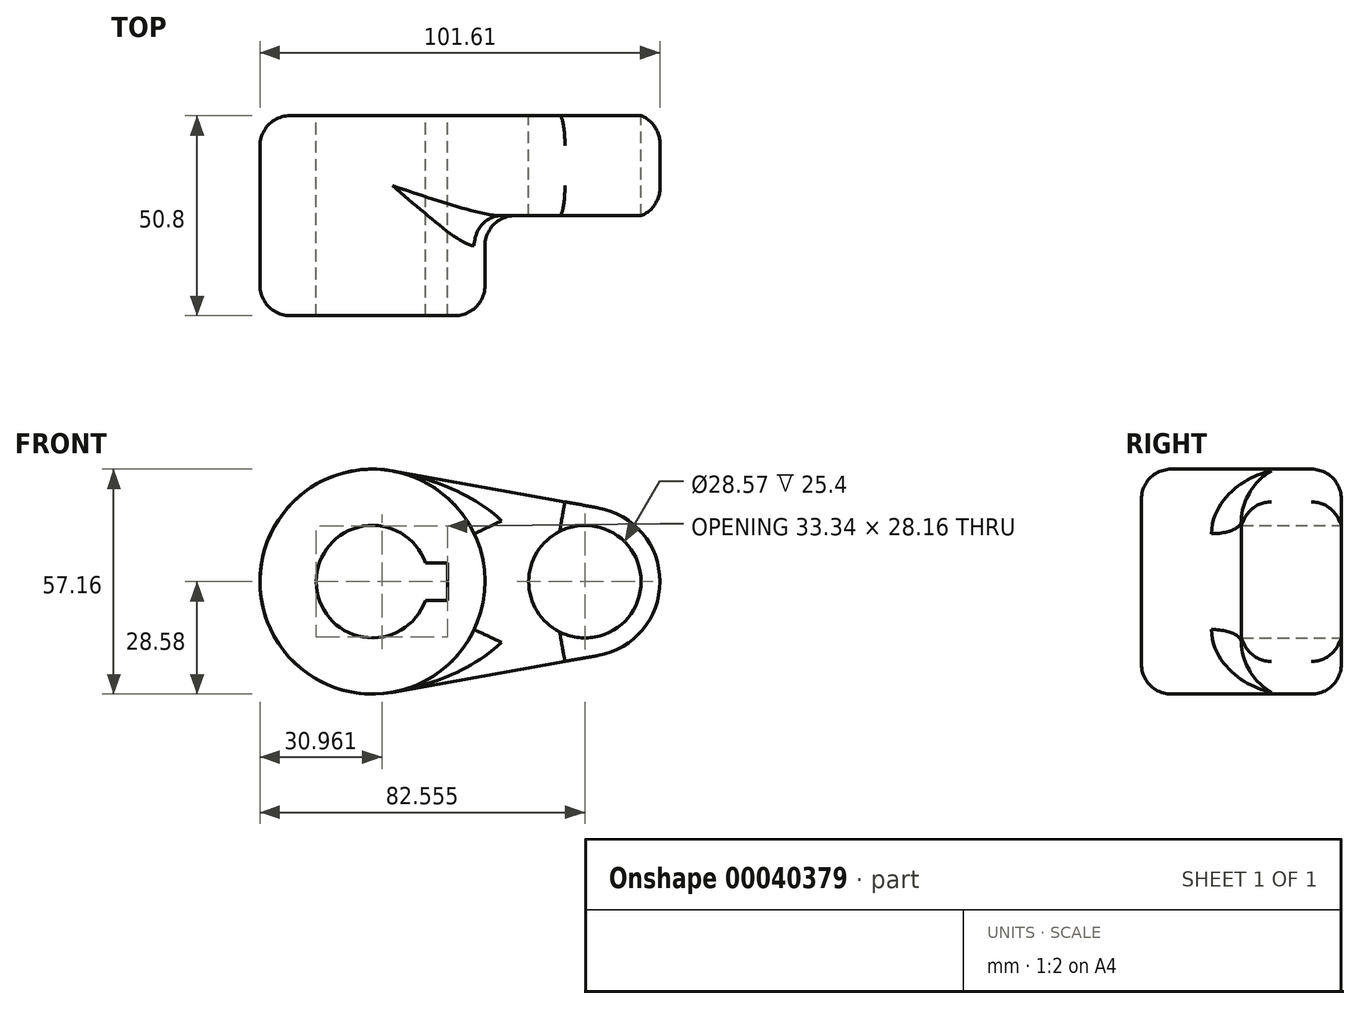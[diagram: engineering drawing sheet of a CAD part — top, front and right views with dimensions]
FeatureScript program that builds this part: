
annotation { "Feature Type Name" : "Feature", "Feature Type Description" : "" }
export const myFeature = defineFeature(function(context is Context, id is Id, definition is map)
    precondition{}
    {
        {
            var Q0;
            Q0=qCreatedBy(makeId("Front.planeOp"),FACE);
            var sketch = newSketch(context, id + "F0", { "sketchPlane" : qUnion([Q0])});
            skCircle(sketch, "E0", {"center": v(0, 0) * mm, "radius": 28.58 * mm});
            skCircle(sketch, "E1", {"center": v(53.98, 0) * mm, "radius": 19.05 * mm});
            skLineSegment(sketch, "E2", {"start": v(5.04, 28.13) * mm, "end": v(57.34, 18.75) * mm});
            skLineSegment(sketch, "E3", {"start": v(5.04, -28.13) * mm, "end": v(57.34, -18.75) * mm});
            skCircle(sketch, "E4", {"center": v(0, 0) * mm, "radius": 14.29 * mm});
            skCircle(sketch, "E5", {"center": v(53.98, 0) * mm, "radius": 14.29 * mm});
            skLineSegment(sketch, "E6.rect.bottom", {"start": v(-19.05, -4.76) * mm, "end": v(19.05, -4.76) * mm});
            skLineSegment(sketch, "E6.rect.top", {"start": v(-19.05, 4.76) * mm, "end": v(19.05, 4.76) * mm});
            skLineSegment(sketch, "E6.rect.left", {"start": v(-19.05, -4.76) * mm, "end": v(-19.05, 4.76) * mm});
            skLineSegment(sketch, "E6.rect.right", {"start": v(19.05, -4.76) * mm, "end": v(19.05, 4.76) * mm});
            skSolve(sketch);
        }
        {
            var Q0;
            {var subQ0=sQuery(id+"F0.wireOp",EDGE,"E6.rect.left");Q0=makeQuery(id+"F0.imprint","IMPRINT",FACE,{"disambiguationData":[TD([[makeQuery(id+"F0.imprint","IMPRINT",EDGE,{"derivedFrom":subQ0}),-1.0]])]});}
            var Q1;
            {var subQ5=sQuery(id+"F0.wireOp",EDGE,"E6.rect.left");Q1=makeQuery(id+"F0.imprint","IMPRINT",FACE,{"disambiguationData":[TD([[makeQuery(id+"F0.imprint","IMPRINT",EDGE,{"derivedFrom":subQ5}),1.0]])]});}
            var Q2;
            Q2=makeQuery(id+"F0.imprint","IMPRINT",FACE,{"disambiguationData":[TD([[makeQuery(id+"F0.imprint","IMPRINT",EDGE,{"derivedFrom":sQuery(id+"F0.wireOp",EDGE,"E5")}),-1.0]])]});
            var Q3;
            {var subQ1=sQuery(id+"F0.wireOp",EDGE,"E2");Q3=makeQuery(id+"F0.imprint","IMPRINT",FACE,{"disambiguationData":[TD([[makeQuery(id+"F0.imprint","IMPRINT",EDGE,{"derivedFrom":subQ1}),-1.0]])]});}
            extrude(context, id + "F1", {"entities" : qUnion([Q0, Q1, Q2, Q3]), "depth" : 25.4 * mm});
        }
        {
            var Q0;
            {var subQ5=sQuery(id+"F0.wireOp",EDGE,"E6.rect.left");Q0=makeQuery(id+"F0.imprint","IMPRINT",FACE,{"disambiguationData":[TD([[makeQuery(id+"F0.imprint","IMPRINT",EDGE,{"derivedFrom":subQ5}),1.0]])]});}
            var Q1;
            {var subQ0=sQuery(id+"F0.wireOp",EDGE,"E6.rect.left");Q1=makeQuery(id+"F0.imprint","IMPRINT",FACE,{"disambiguationData":[TD([[makeQuery(id+"F0.imprint","IMPRINT",EDGE,{"derivedFrom":subQ0}),-1.0]])]});}
            extrude(context, id + "F2", {"entities" : qUnion([Q0, Q1]), "operationType" : NewBodyOperationType.ADD, "depth" : 50.8 * mm});
        }
        {
            var Q0;
            {var subQ0=sQuery(id+"F0.wireOp",EDGE,"E0");Q0=makeQuery(id+"F2.boolean.opBoolean","MERGE",FACE,{"derivedFrom":[makeQuery(id+"F1.opExtrude","SWEPT_FACE",FACE,{"disambiguationData":[OSD([subQ0])]}),makeQuery(id+"F2.opExtrude","SWEPT_FACE",FACE,{"disambiguationData":[OSD([subQ0])]})]});}
            var Q1;
            Q1=makeQuery(id+"F1.opExtrude","CAP_EDGE",EDGE,{"disambiguationData":[OSD([sQuery(id+"F0.wireOp",EDGE,"E2")])],"isStart":false});
            fillet(context, id + "F3", {"entities" : qUnion([Q0, Q1]), "radius" : 7.62 * mm, "tangentPropagation" : true, "allowEdgeOverflow" : false});
        }
    });
